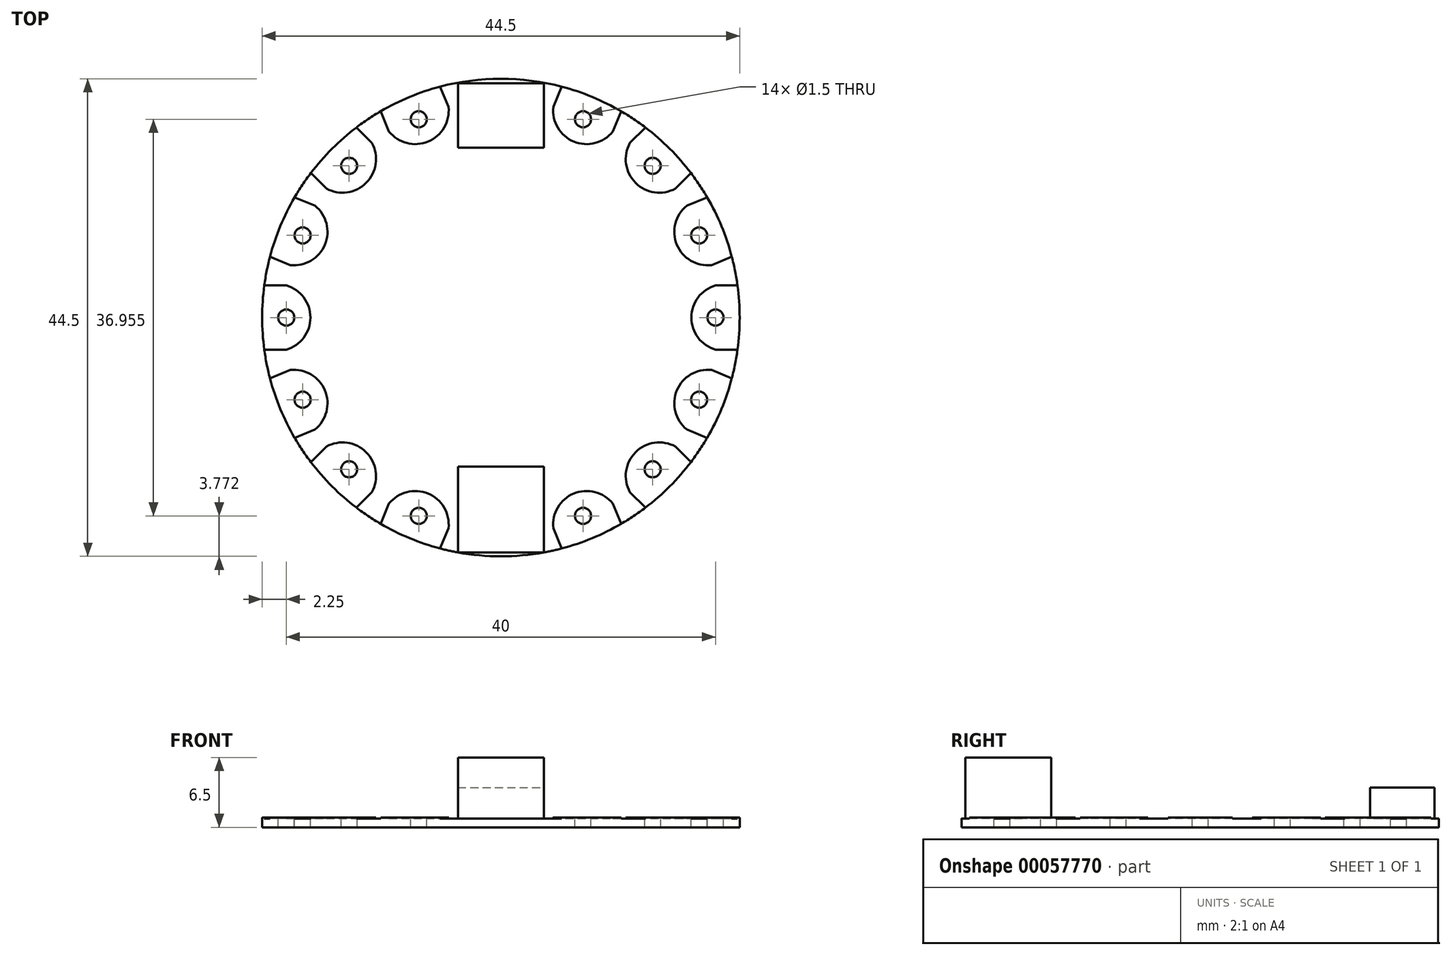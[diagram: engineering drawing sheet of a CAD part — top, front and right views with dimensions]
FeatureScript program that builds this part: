
annotation { "Feature Type Name" : "Feature", "Feature Type Description" : "" }
export const myFeature = defineFeature(function(context is Context, id is Id, definition is map)
    precondition{}
    {
        {
            var Q0;
            Q0=qCreatedBy(makeId("Top.planeOp"),FACE);
            var sketch = newSketch(context, id + "F0", { "sketchPlane" : qUnion([Q0])});
            skCircle(sketch, "E0", {"center": v(0, 0) * mm, "radius": 22.25 * mm});
            skSolve(sketch);
        }
        {
            var Q0;
            Q0=makeQuery(id+"F0.imprint","IMPRINT",FACE,{"disambiguationData":[TD([[makeQuery(id+"F0.imprint","IMPRINT",EDGE,{"derivedFrom":sQuery(id+"F0.wireOp",EDGE,"E0")}),1.0]])]});
            extrude(context, id + "F1", {"entities" : qUnion([Q0]), "depth" : 0.8 * mm});
        }
        {
            var Q0;
            Q0=makeQuery(id+"F1.opExtrude","CAP_FACE",FACE,{"disambiguationData":[OSD([sQuery(id+"F0.wireOp",EDGE,"E0")])],"isStart":false});
            var sketch = newSketch(context, id + "F2", { "sketchPlane" : qUnion([Q0])});
            skLineSegment(sketch, "E1.bottom", {"start": v(-4, -13.89) * mm, "end": v(4, -13.89) * mm});
            skLineSegment(sketch, "E1.top", {"start": v(-4, -21.89) * mm, "end": v(4, -21.89) * mm});
            skLineSegment(sketch, "E1.left", {"start": v(-4, -13.89) * mm, "end": v(-4, -21.89) * mm});
            skLineSegment(sketch, "E1.right", {"start": v(4, -13.89) * mm, "end": v(4, -21.89) * mm});
            skSolve(sketch);
        }
        {
            var Q0;
            Q0=makeQuery(id+"F2.imprint","IMPRINT",FACE,{"disambiguationData":[TD([[makeQuery(id+"F2.imprint","IMPRINT",EDGE,{"derivedFrom":sQuery(id+"F2.wireOp",EDGE,"E1.bottom")}),-1.0]])]});
            extrude(context, id + "F3", {"entities" : qUnion([Q0]), "operationType" : NewBodyOperationType.ADD, "depth" : 5.7 * mm});
        }
        {
            var Q0;
            {var subQ0=sQuery(id+"F0.wireOp",EDGE,"E0");var subQ1=makeQuery(id+"F1.opExtrude","CAP_FACE",FACE,{"disambiguationData":[OSD([subQ0])],"isStart":false});Q0=makeQuery(id+"F3.boolean.opBoolean","SPLIT",FACE,{"disambiguationData":[TD([makeQuery(id+"F1.opExtrude","SWEPT_FACE",FACE,{"disambiguationData":[OSD([subQ0])]}),subQ1,makeQuery(id+"F3.opExtrude","SWEPT_FACE",FACE,{"disambiguationData":[OSD([sQuery(id+"F2.wireOp",EDGE,"E1.bottom")])]}),makeQuery(id+"F3.opExtrude","SWEPT_FACE",FACE,{"disambiguationData":[OSD([sQuery(id+"F2.wireOp",EDGE,"E1.top")])]}),makeQuery(id+"F3.opExtrude","SWEPT_FACE",FACE,{"disambiguationData":[OSD([sQuery(id+"F2.wireOp",EDGE,"E1.left")])]}),makeQuery(id+"F3.opExtrude","SWEPT_FACE",FACE,{"disambiguationData":[OSD([sQuery(id+"F2.wireOp",EDGE,"E1.right")])]})])],"derivedFrom":subQ1});}
            var sketch = newSketch(context, id + "F4", { "sketchPlane" : qUnion([Q0])});
            skLineSegment(sketch, "E2.bottom", {"start": v(-4, 21.82) * mm, "end": v(4, 21.82) * mm});
            skLineSegment(sketch, "E2.top", {"start": v(-4, 15.82) * mm, "end": v(4, 15.82) * mm});
            skLineSegment(sketch, "E2.left", {"start": v(-4, 21.82) * mm, "end": v(-4, 15.82) * mm});
            skLineSegment(sketch, "E2.right", {"start": v(4, 21.82) * mm, "end": v(4, 15.82) * mm});
            skSolve(sketch);
        }
        {
            var Q0;
            Q0=makeQuery(id+"F4.imprint","IMPRINT",FACE,{"disambiguationData":[TD([[makeQuery(id+"F4.imprint","IMPRINT",EDGE,{"derivedFrom":sQuery(id+"F4.wireOp",EDGE,"E2.bottom")}),-1.0]])]});
            extrude(context, id + "F5", {"entities" : qUnion([Q0]), "operationType" : NewBodyOperationType.ADD, "depth" : 2.9 * mm});
        }
        {
            var Q0;
            {var subQ0=sQuery(id+"F0.wireOp",EDGE,"E0");var subQ1=makeQuery(id+"F1.opExtrude","CAP_FACE",FACE,{"disambiguationData":[OSD([subQ0])],"isStart":false});Q0=makeQuery(id+"F3.boolean.opBoolean","SPLIT",FACE,{"disambiguationData":[TD([makeQuery(id+"F1.opExtrude","SWEPT_FACE",FACE,{"disambiguationData":[OSD([subQ0])]}),subQ1,makeQuery(id+"F3.opExtrude","SWEPT_FACE",FACE,{"disambiguationData":[OSD([sQuery(id+"F2.wireOp",EDGE,"E1.bottom")])]}),makeQuery(id+"F3.opExtrude","SWEPT_FACE",FACE,{"disambiguationData":[OSD([sQuery(id+"F2.wireOp",EDGE,"E1.top")])]}),makeQuery(id+"F3.opExtrude","SWEPT_FACE",FACE,{"disambiguationData":[OSD([sQuery(id+"F2.wireOp",EDGE,"E1.left")])]}),makeQuery(id+"F3.opExtrude","SWEPT_FACE",FACE,{"disambiguationData":[OSD([sQuery(id+"F2.wireOp",EDGE,"E1.right")])]})])],"derivedFrom":subQ1});}
            var sketch = newSketch(context, id + "F6", { "sketchPlane" : qUnion([Q0])});
            skArc(sketch, "E3", {"start": v(-20, -3) * mm, "mid": v(-17.75, 0) * mm, "end": v(-20, 3) * mm});
            skPoint(sketch, "E3.first.point", {"position": v(-20, 3) * mm});
            skPoint(sketch, "E3.second.point", {"position": v(-17.75, 0) * mm});
            skPoint(sketch, "E3.third.point", {"position": v(-20, -3) * mm});
            skLineSegment(sketch, "E4", {"start": v(-20, 3) * mm, "end": v(-22.05, 3) * mm});
            skLineSegment(sketch, "E5", {"start": v(-20, -3) * mm, "end": v(-22.05, -3) * mm});
            skCircle(sketch, "E6", {"center": v(-20, 0) * mm, "radius": 0.75 * mm});
            skSolve(sketch);
        }
        {
            var Q0;
            Q0=makeQuery(id+"F6.imprint","IMPRINT",FACE,{"disambiguationData":[TD([[makeQuery(id+"F6.imprint","IMPRINT",EDGE,{"derivedFrom":sQuery(id+"F6.wireOp",EDGE,"E6")}),1.0]])]});
            var Q1;
            Q1=sQuery(id+"F6.wireOp",EDGE,"E6");
            var Q2;
            Q2=makeQuery(id+"F1.opExtrude","SWEPT_BODY",BODY,{"disambiguationData":[OSD([sQuery(id+"F0.wireOp",EDGE,"E0")])]});
            extrude(context, id + "F7", {"entities" : qUnion([Q0]), "operationType" : NewBodyOperationType.REMOVE, "surfaceEntities" : qUnion([Q1]), "endBound" : BoundingType.UP_TO_BODY, "oppositeDirection" : true, "endBoundEntityBody" : qUnion([Q2]), "depth" : 25 * mm});
        }
        {
            var Q0;
            Q0=makeQuery(id+"F6.imprint","IMPRINT",FACE,{"disambiguationData":[TD([[makeQuery(id+"F6.imprint","IMPRINT",EDGE,{"derivedFrom":sQuery(id+"F6.wireOp",EDGE,"E3")}),1.0]])]});
            extrude(context, id + "F8", {"entities" : qUnion([Q0]), "operationType" : NewBodyOperationType.ADD, "depth" : 0.1 * mm});
        }
        {
            var Q0;
            {var subQ0=sQuery(id+"F6.wireOp",EDGE,"E6");Q0=makeQuery(id+"F8.boolean.opBoolean","MERGE",FACE,{"derivedFrom":[makeQuery(id+"F7.boolean.opBoolean","COPY",FACE,{"derivedFrom":makeQuery(id+"F7.opExtrude","SWEPT_FACE",FACE,{"disambiguationData":[OSD([subQ0])]})}),makeQuery(id+"F8.opExtrude","SWEPT_FACE",FACE,{"disambiguationData":[OSD([subQ0])]})]});}
            var Q1;
            Q1=makeQuery(id+"F8.opExtrude","CAP_FACE",FACE,{"disambiguationData":[OSD([sQuery(id+"F0.wireOp",EDGE,"E0"),sQuery(id+"F6.wireOp",EDGE,"E3"),sQuery(id+"F6.wireOp",EDGE,"E4"),sQuery(id+"F6.wireOp",EDGE,"E5"),sQuery(id+"F6.wireOp",EDGE,"E6")])],"isStart":false});
            var Q2;
            Q2=makeQuery(id+"F8.opExtrude","SWEPT_FACE",FACE,{"disambiguationData":[OSD([sQuery(id+"F6.wireOp",EDGE,"E5")])]});
            var Q3;
            Q3=makeQuery(id+"F8.opExtrude","SWEPT_FACE",FACE,{"disambiguationData":[OSD([sQuery(id+"F6.wireOp",EDGE,"E3")])]});
            var Q4;
            Q4=makeQuery(id+"F8.opExtrude","SWEPT_FACE",FACE,{"disambiguationData":[OSD([sQuery(id+"F6.wireOp",EDGE,"E4")])]});
            var Q5;
            Q5=makeQuery(id+"F1.opExtrude","CAP_EDGE",EDGE,{"disambiguationData":[OSD([sQuery(id+"F0.wireOp",EDGE,"E0")])],"isStart":true});
            circularPattern(context, id + "F9", {"faces" : qUnion([Q0, Q1, Q2, Q3, Q4]), "axis" : qUnion([Q5]), "angle" : 7.5 * degree, "instanceCount" : 25, "patternType" : PatternType.FACE});
        }
        {
            var Q0;
            {var subQ0=sQuery(id+"F6.wireOp",EDGE,"E6");Q0=makeQuery(id+"F8.boolean.opBoolean","MERGE",FACE,{"derivedFrom":[makeQuery(id+"F7.boolean.opBoolean","COPY",FACE,{"derivedFrom":makeQuery(id+"F7.opExtrude","SWEPT_FACE",FACE,{"disambiguationData":[OSD([subQ0])]})}),makeQuery(id+"F8.opExtrude","SWEPT_FACE",FACE,{"disambiguationData":[OSD([subQ0])]})]});}
            var Q1;
            Q1=makeQuery(id+"F8.opExtrude","CAP_FACE",FACE,{"disambiguationData":[OSD([sQuery(id+"F0.wireOp",EDGE,"E0"),sQuery(id+"F6.wireOp",EDGE,"E3"),sQuery(id+"F6.wireOp",EDGE,"E4"),sQuery(id+"F6.wireOp",EDGE,"E5"),sQuery(id+"F6.wireOp",EDGE,"E6")])],"isStart":false});
            var Q2;
            Q2=makeQuery(id+"F8.opExtrude","SWEPT_FACE",FACE,{"disambiguationData":[OSD([sQuery(id+"F6.wireOp",EDGE,"E5")])]});
            var Q3;
            Q3=makeQuery(id+"F8.opExtrude","SWEPT_FACE",FACE,{"disambiguationData":[OSD([sQuery(id+"F6.wireOp",EDGE,"E3")])]});
            var Q4;
            Q4=makeQuery(id+"F8.opExtrude","SWEPT_FACE",FACE,{"disambiguationData":[OSD([sQuery(id+"F6.wireOp",EDGE,"E4")])]});
            var Q5;
            Q5=makeQuery(id+"F1.opExtrude","CAP_EDGE",EDGE,{"disambiguationData":[OSD([sQuery(id+"F0.wireOp",EDGE,"E0")])],"isStart":true});
            circularPattern(context, id + "F10", {"faces" : qUnion([Q0, Q1, Q2, Q3, Q4]), "axis" : qUnion([Q5]), "angle" : 7.5 * degree, "instanceCount" : 10, "oppositeDirection" : true, "patternType" : PatternType.FACE});
        }
        {
            var Q0;
            {var subQ0=sQuery(id+"F6.wireOp",EDGE,"E6");Q0=makeQuery(id+"F9.opPattern","COPY",FACE,{"derivedFrom":makeQuery(id+"F8.boolean.opBoolean","MERGE",FACE,{"derivedFrom":[makeQuery(id+"F7.boolean.opBoolean","COPY",FACE,{"derivedFrom":makeQuery(id+"F7.opExtrude","SWEPT_FACE",FACE,{"disambiguationData":[OSD([subQ0])]})}),makeQuery(id+"F8.opExtrude","SWEPT_FACE",FACE,{"disambiguationData":[OSD([subQ0])]})]}),"instanceName":"24"});}
            var Q1;
            Q1=makeQuery(id+"F9.opPattern","COPY",FACE,{"derivedFrom":makeQuery(id+"F8.opExtrude","CAP_FACE",FACE,{"disambiguationData":[OSD([sQuery(id+"F0.wireOp",EDGE,"E0"),sQuery(id+"F6.wireOp",EDGE,"E3"),sQuery(id+"F6.wireOp",EDGE,"E4"),sQuery(id+"F6.wireOp",EDGE,"E5"),sQuery(id+"F6.wireOp",EDGE,"E6")])],"isStart":false}),"instanceName":"24"});
            var Q2;
            Q2=makeQuery(id+"F9.opPattern","COPY",FACE,{"derivedFrom":makeQuery(id+"F8.opExtrude","SWEPT_FACE",FACE,{"disambiguationData":[OSD([sQuery(id+"F6.wireOp",EDGE,"E4")])]}),"instanceName":"24"});
            var Q3;
            Q3=makeQuery(id+"F9.opPattern","COPY",FACE,{"derivedFrom":makeQuery(id+"F8.opExtrude","SWEPT_FACE",FACE,{"disambiguationData":[OSD([sQuery(id+"F6.wireOp",EDGE,"E3")])]}),"instanceName":"24"});
            var Q4;
            Q4=makeQuery(id+"F9.opPattern","COPY",FACE,{"derivedFrom":makeQuery(id+"F8.opExtrude","SWEPT_FACE",FACE,{"disambiguationData":[OSD([sQuery(id+"F6.wireOp",EDGE,"E5")])]}),"instanceName":"24"});
            var Q5;
            Q5=makeQuery(id+"F1.opExtrude","CAP_EDGE",EDGE,{"disambiguationData":[OSD([sQuery(id+"F0.wireOp",EDGE,"E0")])],"isStart":true});
            circularPattern(context, id + "F11", {"faces" : qUnion([Q0, Q1, Q2, Q3, Q4]), "axis" : qUnion([Q5]), "angle" : 7.5 * degree, "instanceCount" : 10, "patternType" : PatternType.FACE});
        }
    });
